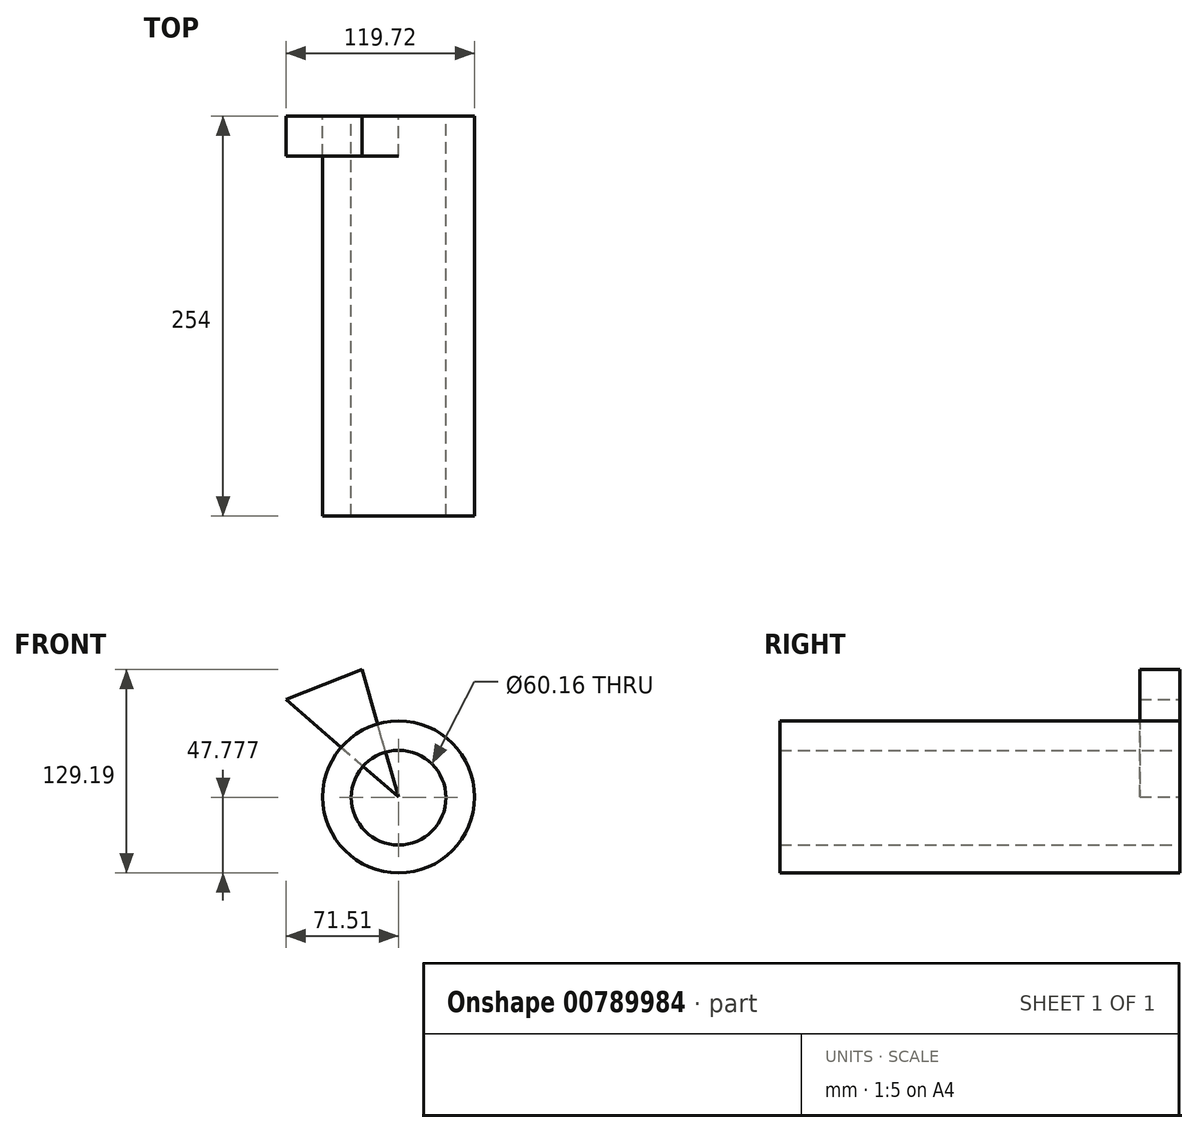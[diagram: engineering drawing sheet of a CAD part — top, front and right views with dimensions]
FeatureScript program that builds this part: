
annotation { "Feature Type Name" : "Feature", "Feature Type Description" : "" }
export const myFeature = defineFeature(function(context is Context, id is Id, definition is map)
    precondition{}
    {
        {
            var Q0;
            Q0=qCreatedBy(makeId("Front.planeOp"),FACE);
            var sketch = newSketch(context, id + "F0", { "sketchPlane" : qUnion([Q0])});
            skLineSegment(sketch, "E0", {"start": v(-71.5, 61.87) * mm, "end": v(0, 0) * mm});
            skLineSegment(sketch, "E1", {"start": v(0, 0) * mm, "end": v(-23.39, 80.98) * mm});
            skLineSegment(sketch, "E2", {"start": v(-23.39, 80.98) * mm, "end": v(-71.5, 61.87) * mm});
            skLineSegment(sketch, "E3", {"start": v(-35.75, 30.93) * mm, "end": v(-28.58, 22.52) * mm, "construction": true});
            skLineSegment(sketch, "E4", {"start": v(-28.58, 22.52) * mm, "end": v(-55, 0) * mm, "construction": true});
            skSolve(sketch);
        }
        {
            var Q0;
            Q0 = qSketchRegion(id + "F0", true);
            extrude(context, id + "F1", {"entities" : qUnion([Q0]), "depth" : 25.4 * mm, "offsetDistance" : 25.4 * mm});
        }
        {
            var Q0;
            Q0=qCreatedBy(makeId("Front.planeOp"),FACE);
            var sketch = newSketch(context, id + "F2", { "sketchPlane" : qUnion([Q0])});
            skCircle(sketch, "E5", {"center": v(0, 0) * mm, "radius": 48.21 * mm});
            skCircle(sketch, "E6", {"center": v(0, -0.43) * mm, "radius": 30.08 * mm});
            skSolve(sketch);
        }
        {
            var Q0;
            Q0 = qSketchRegion(id + "F2", true);
            extrude(context, id + "F3", {"entities" : qUnion([Q0]), "depth" : 254 * mm, "offsetDistance" : 25.4 * mm});
        }
    });
